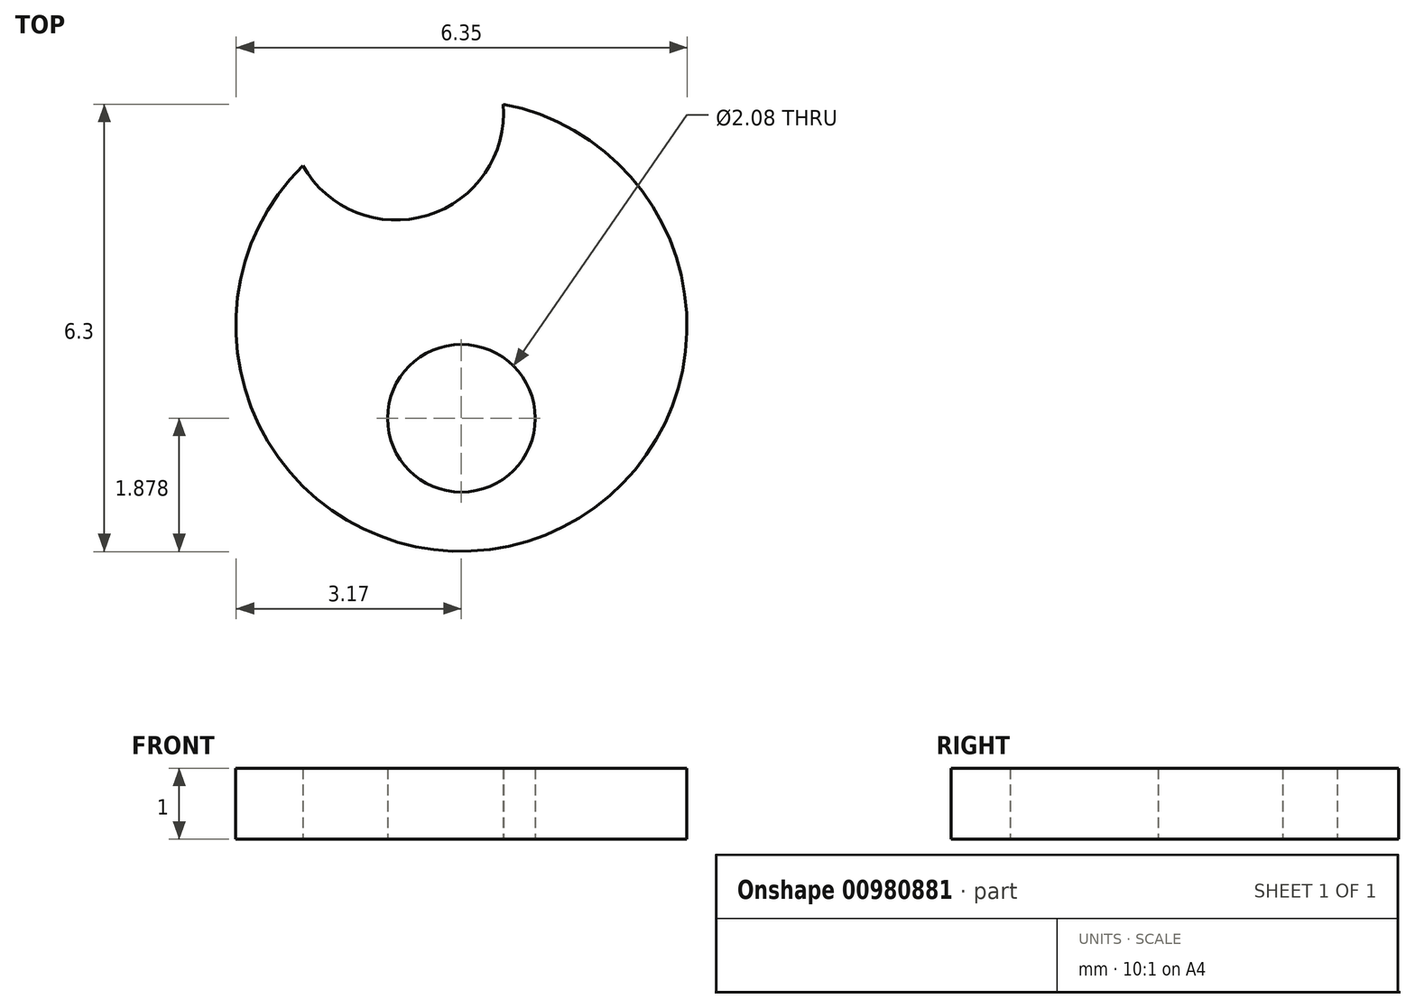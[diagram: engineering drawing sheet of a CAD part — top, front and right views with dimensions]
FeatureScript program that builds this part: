
annotation { "Feature Type Name" : "Feature", "Feature Type Description" : "" }
export const myFeature = defineFeature(function(context is Context, id is Id, definition is map)
    precondition{}
    {
        {
            var Q0;
            Q0=qCreatedBy(makeId("Top.planeOp"),FACE);
            var sketch = newSketch(context, id + "F0", { "sketchPlane" : qUnion([Q0])});
            skCircle(sketch, "E0", {"center": v(0, 0) * mm, "radius": 3.17 * mm});
            skCircle(sketch, "E1", {"center": v(0, -1.3) * mm, "radius": 1.04 * mm});
            skCircle(sketch, "E2", {"center": v(-0.92, 3) * mm, "radius": 1.51 * mm});
            skSolve(sketch);
        }
        {
            var Q0;
            Q0=makeQuery(id+"F0.imprint","IMPRINT",FACE,{"disambiguationData":[TD([[makeQuery(id+"F0.imprint","IMPRINT",EDGE,{"derivedFrom":sQuery(id+"F0.wireOp",EDGE,"E1")}),-1.0]])]});
            extrude(context, id + "F1", {"entities" : qUnion([Q0]), "depth" : 1 * mm, "offsetDistance" : 25 * mm});
        }
    });
